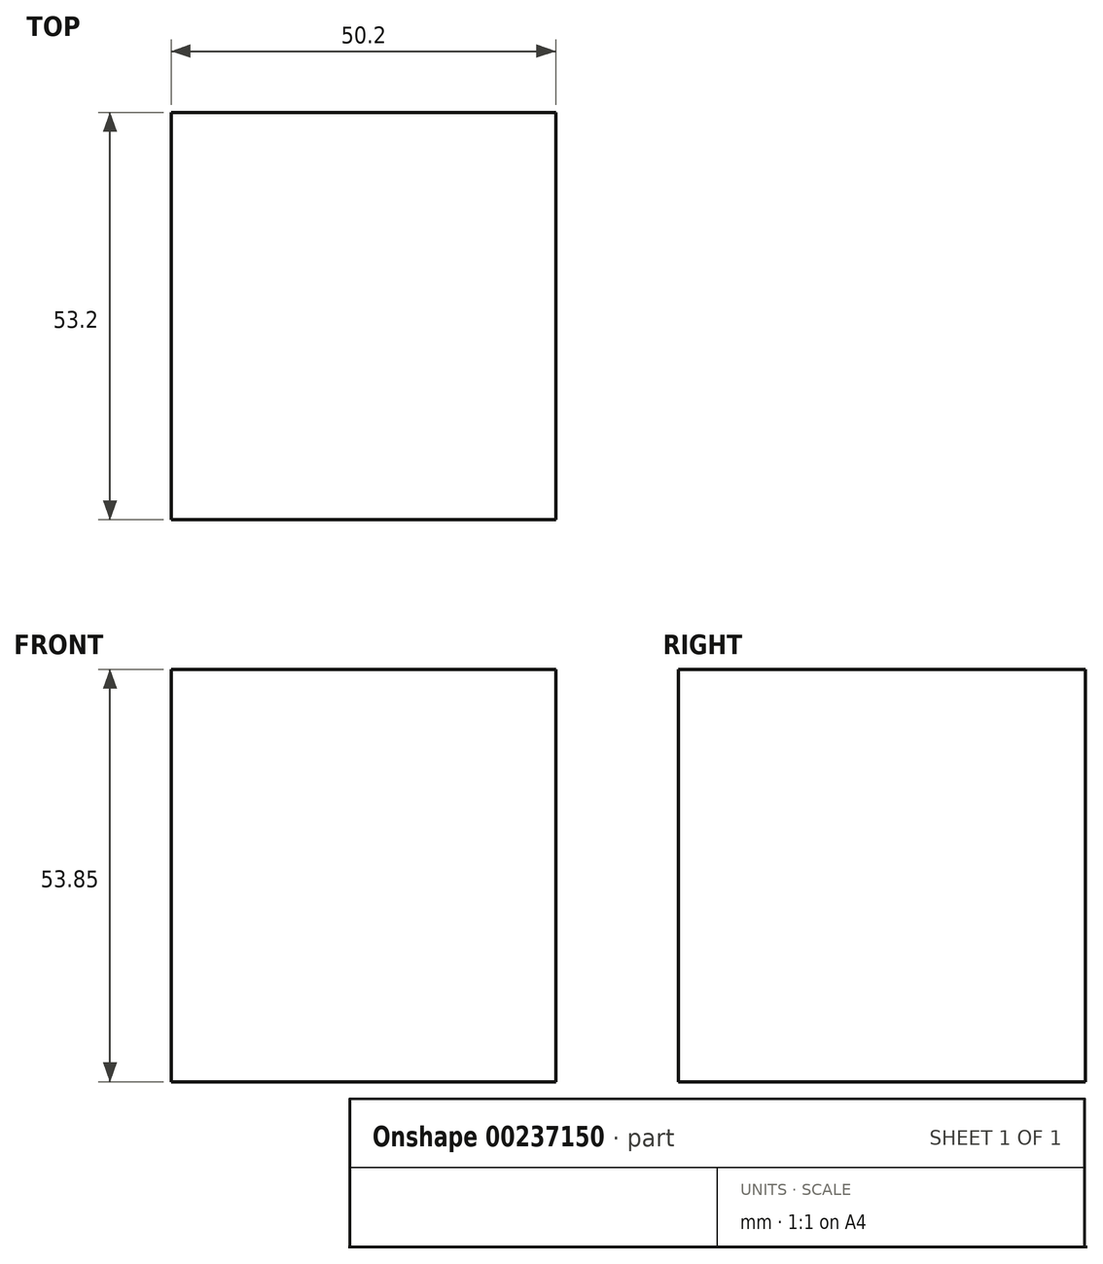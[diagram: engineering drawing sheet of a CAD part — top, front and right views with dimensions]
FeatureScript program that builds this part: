
annotation { "Feature Type Name" : "Feature", "Feature Type Description" : "" }
export const myFeature = defineFeature(function(context is Context, id is Id, definition is map)
    precondition{}
    {
        {
            var Q0;
            Q0=qCreatedBy(makeId("Top.planeOp"),FACE);
            var sketch = newSketch(context, id + "F0", { "sketchPlane" : qUnion([Q0])});
            skLineSegment(sketch, "E0.bottom", {"start": v(0, 0) * mm, "end": v(50.2, 0) * mm});
            skLineSegment(sketch, "E0.top", {"start": v(0, 53.2) * mm, "end": v(50.2, 53.2) * mm});
            skLineSegment(sketch, "E0.left", {"start": v(0, 0) * mm, "end": v(0, 53.2) * mm});
            skLineSegment(sketch, "E0.right", {"start": v(50.2, 0) * mm, "end": v(50.2, 53.2) * mm});
            skSolve(sketch);
        }
        {
            var Q0;
            Q0=makeQuery(id+"F0.imprint","IMPRINT",FACE,{"disambiguationData":[TD([[makeQuery(id+"F0.imprint","IMPRINT",EDGE,{"derivedFrom":sQuery(id+"F0.wireOp",EDGE,"E0.bottom")}),1.0]])]});
            extrude(context, id + "F1", {"entities" : qUnion([Q0]), "depth" : 53.85 * mm});
        }
    });
